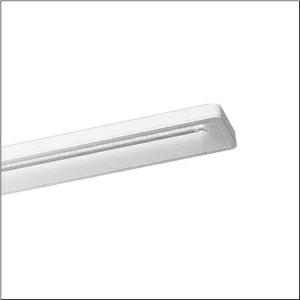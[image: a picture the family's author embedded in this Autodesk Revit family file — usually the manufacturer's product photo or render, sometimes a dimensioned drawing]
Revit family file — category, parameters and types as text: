
# Revit family: taris_r__21_5mt217704wd_5e77
name_source: partatom
category: Lighting Fixtures
units: mm (PartAtom-declared; Revit-internal decimal feet)

## family parameters
Cut with Voids When Loaded = No
Host = Face
Light Source = No
Part Type = Normal
Room Calculation Point = No
Round Connector Dimension = Use Diameter
Shared = No

## types (1)
- Taris® 21 (1 x LED, 6140 lm, 37 W, 4000K)
    Apparent Load = 37 VA
    CIE Flux Codes = 73 96 99 100 100
    Color Rendering = 80
    Color Temperature = 4000K
    Default Elevation = 1800 mm
    Description = Taris® 21, office luminaire, primary anti-glare with micro louvre, primary optical cover: axial lens, of PMMA, structured, CAT 2 (L<= 1500cd/m²), light emission: direct distribution, primary light characteristic: symmetric, installation type: surface-mounted, LED, rated luminous flux: 6.140lm, luminous efficacy: 166lm/W, light colour: 840, colour temperature: 4000K, control gear: ECG, with terminal, 5-pole, mains connection: 230V, AC, 50Hz, rated input power: 37W, housing, luminaire housing, of plastic, traffic white (RAL 9016), length: 1.510mm, width: 134mm, height: 50mm, protection rating (complete): IP20, insulation class (complete): insulation class I (protective earthing), certification: CE, ENEC, VDE, protection symbol: F, impact resistance: IK02, permissible operating ambient temperature: 0..+35°C, standard: EN 50419, packaging unit: 1 piece
    Height = 51 mm
    Lamp = 1 x LED
    Lamp Light Flux = 6140 lm
    Lamp Power = 37 W
    Lamp count = 1
    Length = 1514 mm
    Luminous efficacy = 166 lm/W
    Manufacturer = Siteco
    ModVariant = No
    Model = 5MT217704WD
    Mounting Place = Ceiling
    Mounting Type = Surface mounted
    Number of Poles = 1
    OnlyDefault = Yes
    Power Factor = 1
    Product Name = Taris® 21
    Product group = office luminaire | ceiling mounted
    ProductGroupID = 304
    Protection Class = Protection class I
    Protection Degree = IP 20
    RLX_Detail_Level = 1
    RLX_Emergency_Light_Flux = 0 lm
    RLX_Emergency_Type = 0
    RLX_Emergency_Type_DB = No
    RlxData = <blob elided: 39013 chars, md5=1b1aabce>
    Socket = socket
    Standby Power = 0 W
    System Light Flux = 6140 lm
    System Power = 37 W
    Type Comments = Product without accessories
    Type Image = l_1004728.jpg
    URL = http://relux.com
    VarID = ---
    Voltage = 0 V
    Weight = 0.00 kg
    Width = 134 mm

## geometry (parser evidence)
native form markers: Blend x4, Sweep x10
no freeform markers — native parametric forms only
